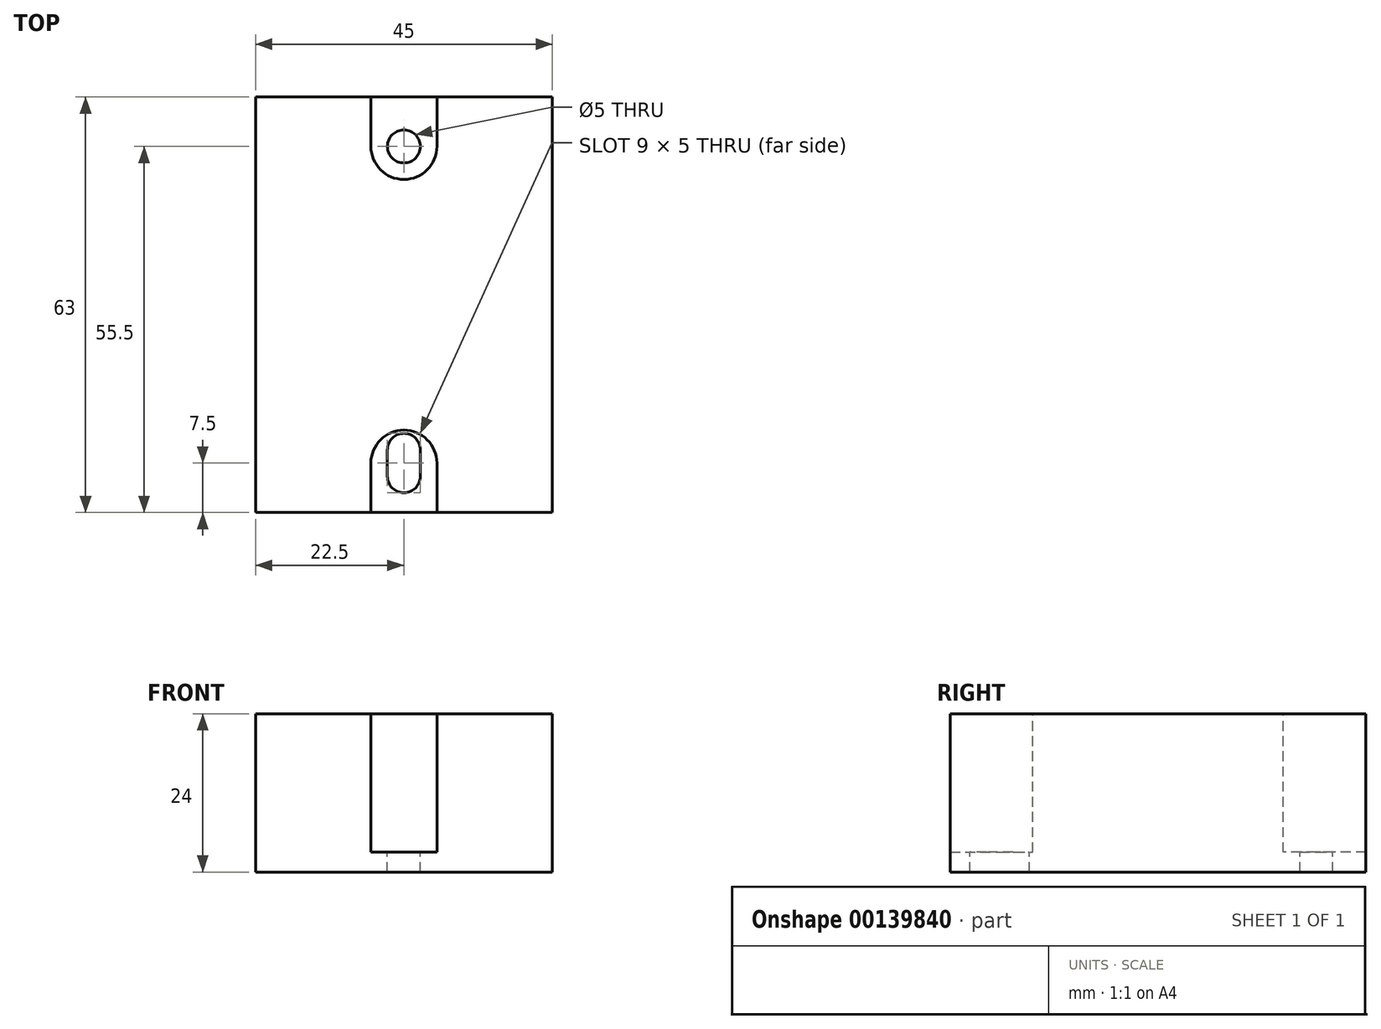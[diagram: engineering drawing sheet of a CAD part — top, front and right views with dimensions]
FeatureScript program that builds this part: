
annotation { "Feature Type Name" : "Feature", "Feature Type Description" : "" }
export const myFeature = defineFeature(function(context is Context, id is Id, definition is map)
    precondition{}
    {
        {
            var Q0;
            Q0=qCreatedBy(makeId("Top.planeOp"),FACE);
            var sketch = newSketch(context, id + "F0", { "sketchPlane" : qUnion([Q0])});
            skLineSegment(sketch, "E0.bottom", {"start": v(22.5, 31.5) * mm, "end": v(-22.5, 31.5) * mm});
            skLineSegment(sketch, "E0.top", {"start": v(22.5, -31.5) * mm, "end": v(-22.5, -31.5) * mm});
            skLineSegment(sketch, "E0.left", {"start": v(22.5, 31.5) * mm, "end": v(22.5, -31.5) * mm});
            skLineSegment(sketch, "E0.right", {"start": v(-22.5, 31.5) * mm, "end": v(-22.5, -31.5) * mm});
            skPoint(sketch, "E0.middle", {"position": v(0, 0) * mm});
            skSolve(sketch);
        }
        {
            var Q0;
            Q0 = qSketchRegion(id + "F0", true);
            extrude(context, id + "F1", {"entities" : qUnion([Q0]), "depth" : 24 * mm});
        }
        {
            var Q0;
            Q0=makeQuery(id+"F1.opExtrude","CAP_FACE",FACE,{"disambiguationData":[OSD([sQuery(id+"F0.wireOp",EDGE,"E0.bottom"),sQuery(id+"F0.wireOp",EDGE,"E0.top"),sQuery(id+"F0.wireOp",EDGE,"E0.left"),sQuery(id+"F0.wireOp",EDGE,"E0.right")])],"isStart":false});
            var sketch = newSketch(context, id + "F2", { "sketchPlane" : qUnion([Q0])});
            skLineSegment(sketch, "E1", {"start": v(-5, 31.5) * mm, "end": v(5, 31.5) * mm});
            skLineSegment(sketch, "E2", {"start": v(5, 31.5) * mm, "end": v(5, 24) * mm});
            skLineSegment(sketch, "E3", {"start": v(-5, 31.5) * mm, "end": v(-5, 24) * mm});
            skArc(sketch, "E4", {"start": v(-5, 24) * mm, "mid": v(0, 19) * mm, "end": v(5, 24) * mm});
            skLineSegment(sketch, "E5.MirrorCS", {"start": v(-5, -31.5) * mm, "end": v(-5, -24) * mm});
            skLineSegment(sketch, "E6.MirrorCS", {"start": v(-5, -31.5) * mm, "end": v(5, -31.5) * mm});
            skLineSegment(sketch, "E7.MirrorCS", {"start": v(5, -31.5) * mm, "end": v(5, -24) * mm});
            skArc(sketch, "E8.MirrorCS", {"start": v(-5, -24) * mm, "mid": v(0, -19) * mm, "end": v(5, -24) * mm});
            skSolve(sketch);
        }
        {
            var Q0;
            Q0=makeQuery(id+"F2.imprint","IMPRINT",FACE,{"disambiguationData":[TD([[makeQuery(id+"F2.imprint","IMPRINT",EDGE,{"derivedFrom":sQuery(id+"F2.wireOp",EDGE,"E1")}),1.0]])]});
            var Q1;
            Q1=makeQuery(id+"F2.imprint","IMPRINT",FACE,{"disambiguationData":[TD([[makeQuery(id+"F2.imprint","IMPRINT",EDGE,{"derivedFrom":sQuery(id+"F2.wireOp",EDGE,"E5.MirrorCS")}),-1.0]])]});
            extrude(context, id + "F3", {"entities" : qUnion([Q0, Q1]), "operationType" : NewBodyOperationType.REMOVE, "oppositeDirection" : true, "depth" : 21 * mm});
        }
        {
            var Q0;
            Q0=makeQuery(id+"F3.boolean.opBoolean","COPY",FACE,{"derivedFrom":makeQuery(id+"F3.opExtrude","CAP_FACE",FACE,{"disambiguationData":[OSD([sQuery(id+"F2.wireOp",EDGE,"E1"),sQuery(id+"F2.wireOp",EDGE,"E2"),sQuery(id+"F2.wireOp",EDGE,"E3"),sQuery(id+"F2.wireOp",EDGE,"E4")])],"isStart":false})});
            var sketch = newSketch(context, id + "F4", { "sketchPlane" : qUnion([Q0])});
            skCircle(sketch, "E9", {"center": v(0, 24) * mm, "radius": 2.5 * mm});
            skArc(sketch, "E10", {"start": v(2.5, -22) * mm, "mid": v(0, -19.5) * mm, "end": v(-2.5, -22) * mm});
            skArc(sketch, "E11", {"start": v(-2.5, -26) * mm, "mid": v(0, -28.5) * mm, "end": v(2.5, -26) * mm});
            skLineSegment(sketch, "E12", {"start": v(-2.5, -22) * mm, "end": v(-2.5, -26) * mm});
            skLineSegment(sketch, "E13", {"start": v(2.5, -22) * mm, "end": v(2.5, -26) * mm});
            skSolve(sketch);
        }
        {
            var Q0;
            Q0=makeQuery(id+"F4.imprint","IMPRINT",FACE,{"disambiguationData":[TD([[makeQuery(id+"F4.imprint","IMPRINT",EDGE,{"derivedFrom":sQuery(id+"F4.wireOp",EDGE,"E9")}),1.0]])]});
            var Q1;
            Q1=makeQuery(id+"F4.imprint","IMPRINT",FACE,{"disambiguationData":[TD([[makeQuery(id+"F4.imprint","IMPRINT",EDGE,{"derivedFrom":sQuery(id+"F4.wireOp",EDGE,"E10")}),1.0]])]});
            extrude(context, id + "F5", {"entities" : qUnion([Q0, Q1]), "operationType" : NewBodyOperationType.REMOVE, "endBound" : BoundingType.UP_TO_NEXT, "oppositeDirection" : true, "depth" : 25 * mm});
        }
    });
